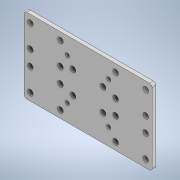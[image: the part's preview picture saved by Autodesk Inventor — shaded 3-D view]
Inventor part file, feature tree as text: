
AUTODESK INVENTOR PART (.ipt)
format: ipt  version: 2020 (Build 240168000, 168)  size: 183,808 bytes
history: native  units: mm
features: extrude x4, sketch x4, pattern_linear x1, mirror x1, fillet x1
ambient origin geometry x8: Origin, YZ Plane, XZ Plane, XY Plane, X Axis, Y Axis, Z Axis, Center Point
bodies: Solid1 (feature_tree)
feature tree (11):
  extrude  "Extrusion1"  Depth=3.0mm TaperAngle=0.0deg
  extrude  "Extrusion2"  Depth=60.0mm
  pattern_linear  "Rectangular Pattern1"  Spacing1=5.0mm  [1 undecoded]
  extrude  "Extrusion3"  Depth=2.0mm
  extrude  "Extrusion4"  Depth=2.0mm
  mirror  "Mirror1"
  fillet  "Fillet1"  Radius=4.5mm
  sketch  "Sketch1"  dims[d0=102.0mm d1=3.0mm d2=0.0mm]
  sketch  "Sketch2"  dims[d3=60.0mm d4=24.0mm]
  sketch  "Sketch3"  dims[d5=18.0mm]
  sketch  "Sketch4"  dims[d6=15.0mm d7=5.0mm d8=4.5mm d9=4.5mm d10=4.5mm d11=4.5mm d12=3.0mm d13=0.0mm d14=20.0mm d16=30.0mm d17=10.0mm d19=86.0mm d20=24.0mm d21=18.0mm d22=4.5mm d23=4.5mm d24=4.5mm d25=4.5mm d26=3.0mm d27=0.0mm d28=33.0mm d29=33.0mm d30=3.3mm d31=3.3mm d32=3.3mm d33=3.3mm d34=3.0mm d35=0.0mm d36=2.0mm]
note: 1 required parameter value undecoded (feature->parameter linkage not recoverable at this tier; creation-order binding heuristic only, values carry confidence <= 0.55)
